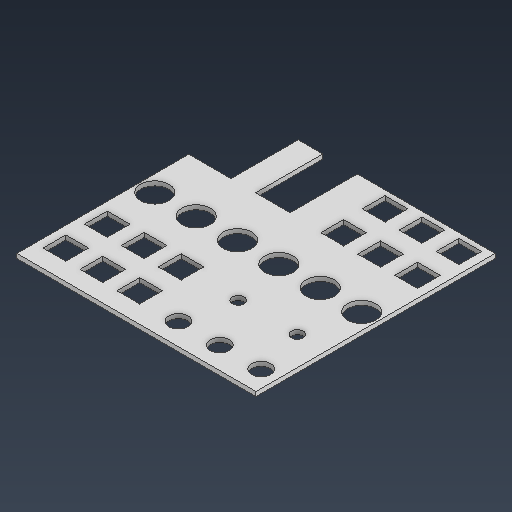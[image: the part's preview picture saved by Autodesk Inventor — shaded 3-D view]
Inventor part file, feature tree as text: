
AUTODESK INVENTOR PART (.ipt)
format: ipt  version: 2025.3 (Build 293356000, 356)  size: 937,984 bytes
history: native  units: mm
features: projected_geometry x26, sketch x21, extrude x10, fillet x1
ambient origin geometry x8: Origin, YZ Plane, XZ Plane, XY Plane, X Axis, Y Axis, Z Axis, Center Point
bodies: Solid1 (feature_tree), Solid2 (feature_tree)
feature tree (58):
  extrude  "Extrusion1"  Depth=171.0mm
  sketch  "Sketch3"  dims[d10=78.0mm d11=78.0mm]
  extrude  "Extrusion3"  Depth=60.0mm
  extrude  "Extrusion5"  Depth=78.0mm
  extrude  "Extrusion6"  Depth=75.0mm
  extrude  "Extrusion7"  Depth=30.0mm
  extrude  "Extrusion8"  Depth=5.0mm
  extrude  "Extrusion9"  Depth=5.0mm
  fillet  "Fillet1"  Radius=25.0mm
  extrude  "Extrusion10"  Depth=15.4mm
  extrude  "Extrusion11"  Depth=12.6mm
  extrude  "Extrusion12"  Depth=4.0mm
  sketch  "Sketch1"  dims[d0=171.0mm d1=171.0mm]
  sketch  "Sketch Rectangular Pattern1"  dims[d2=3.0mm d3=0.0mm d9=60.0mm]
  sketch  "Sketch Rectangular Pattern4"  dims[d12=60.0mm d17=75.0mm]
  sketch  "Sketch5"  dims[d20=5.0mm d21=30.0mm]
  sketch  "Sketch7"  dims[d32=15.4mm d33=15.4mm]
  projected_geometry  "Projected Loop3"
  sketch  "Sketch Rectangular Pattern5"  dims[d22=5.0mm d23=5.0mm]
  sketch  "Sketch8"  dims[d44=6.3mm d45=4.0mm]
  projected_geometry  "Projected Loop4"
  sketch  "Sketch Rectangular Pattern6"  dims[d27=5.0mm d28=5.0mm d31=25.0mm]
  sketch  "Sketch Rectangular Pattern7"  dims[d35=20.0mm d37=28.0mm d38=30.0mm d40=25.0mm d43=12.6mm]
  sketch  "Sketch Rectangular Pattern9"  dims[d46=14.0mm]
  sketch  "Sketch9"  dims[d47=11.7mm]
  projected_geometry  "Projected Loop5"
  projected_geometry  "Projected Loop6"
  projected_geometry  "Projected Loop7"
  projected_geometry  "Projected Loop8"
  projected_geometry  "Projected Loop9"
  projected_geometry  "Projected Loop10"
  projected_geometry  "Projected Loop11"
  projected_geometry  "Projected Loop12"
  sketch  "Sketch Rectangular Pattern11"  dims[d52=15.4mm d53=15.4mm d54=28.0mm d55=25.0mm]
  sketch  "Sketch Rectangular Pattern15"  dims[d58=80.0mm]
  projected_geometry  "Projected Loop26"
  projected_geometry  "Projected Loop27"
  projected_geometry  "Projected Loop28"
  projected_geometry  "Projected Loop29"
  projected_geometry  "Projected Loop30"
  projected_geometry  "Projected Loop31"
  projected_geometry  "Projected Loop32"
  projected_geometry  "Projected Loop33"
  projected_geometry  "Projected Loop34"
  projected_geometry  "Projected Loop35"
  projected_geometry  "Projected Loop36"
  projected_geometry  "Projected Loop37"
  projected_geometry  "Projected Loop38"
  projected_geometry  "Projected Loop39"
  projected_geometry  "Projected Loop40"
  projected_geometry  "Projected Loop41"
  sketch  "Sketch Rectangular Pattern16"  dims[d59=25.0mm]
  sketch  "Sketch Rectangular Pattern17"  dims[d60=25.0mm]
  sketch  "Sketch Rectangular Pattern18"  dims[d61=20.0mm]
  sketch  "Sketch Rectangular Pattern19"  dims[d62=40.0mm d63=8.0mm d64=8.0mm d65=10.0mm d66=0.0mm d67=80.0mm d68=16.2mm d69=16.2mm d70=16.2mm d71=28.0mm d72=28.0mm d73=12.0mm d74=12.8mm d75=12.8mm d76=12.8mm d77=13.0mm d78=60.0mm d80=28.0mm d81=10.0mm d83=10.0mm d85=11.5mm d86=163.0mm d87=65.0mm d88=95.0mm d89=88.0mm d90=13.0mm d91=13.0mm d92=30.0mm d93=40.0mm d94=17.5mm d99=13.0mm d100=28.8mm d101=17.2mm d102=17.2mm d103=1.0mm d104=0.0mm d105=4.0mm d106=4.0mm d107=4.0mm d108=4.0mm d109=4.0mm d110=4.0mm d111=7.0mm d112=4.0mm d113=4.0mm d114=4.0mm d115=4.5mm d116=5.0mm d117=22.0mm d118=12.0mm d119=6.0mm d120=10.0mm d121=0.0mm d122=3.0mm d123=60.0mm d125=28.0mm d126=10.0mm d128=10.0mm d130=3.0mm d131=3.0mm d132=3.0mm d133=3.0mm d134=3.0mm d135=10.0mm d136=6.0mm d137=80.0mm d139=20.0mm d140=10.0mm d142=10.0mm d145=10.0mm d146=40.0mm d148=20.0mm d149=10.0mm d151=10.0mm d153=16.0mm d154=10.0mm d162=10.0mm d163=16.0mm d164=5.0mm d165=0.0mm d166=30.0mm d168=20.0mm d169=10.0mm d171=10.0mm d181=10.0mm d182=80.0mm d184=20.0mm d185=10.0mm d187=10.0mm d215=10.0mm d216=0.0mm d217=6.0mm d218=70.0mm d220=20.0mm d221=10.0mm d223=10.0mm d225=10.0mm d226=10.0mm d227=10.0mm d228=10.0mm d229=10.0mm d230=10.0mm d231=10.0mm d232=10.0mm d233=30.0mm d235=20.0mm d236=10.0mm d238=10.0mm d240=40.0mm d242=20.0mm d243=10.0mm d245=10.0mm d247=30.0mm d249=20.0mm d250=10.0mm d252=10.0mm d254=30.0mm d256=20.0mm d257=10.0mm d259=10.0mm d261=2.7mm d262=10.0mm d263=0.0mm d264=1.0mm d265=3.0mm d266=2.0mm d267=0.0mm d268=0.1mm d269=0.1mm d270=0.1mm d271=0.1mm d272=0.1mm d273=0.1mm d274=0.1mm d275=10.0mm d276=0.0mm d277=10.0mm d278=0.0mm]
  sketch  "Sketch10"  dims[d49=20.0mm d51=30.0mm]
  sketch  "Sketch11"  dims[d56=12.6mm]
  sketch  "Sketch12"  dims[d57=30.0mm]
